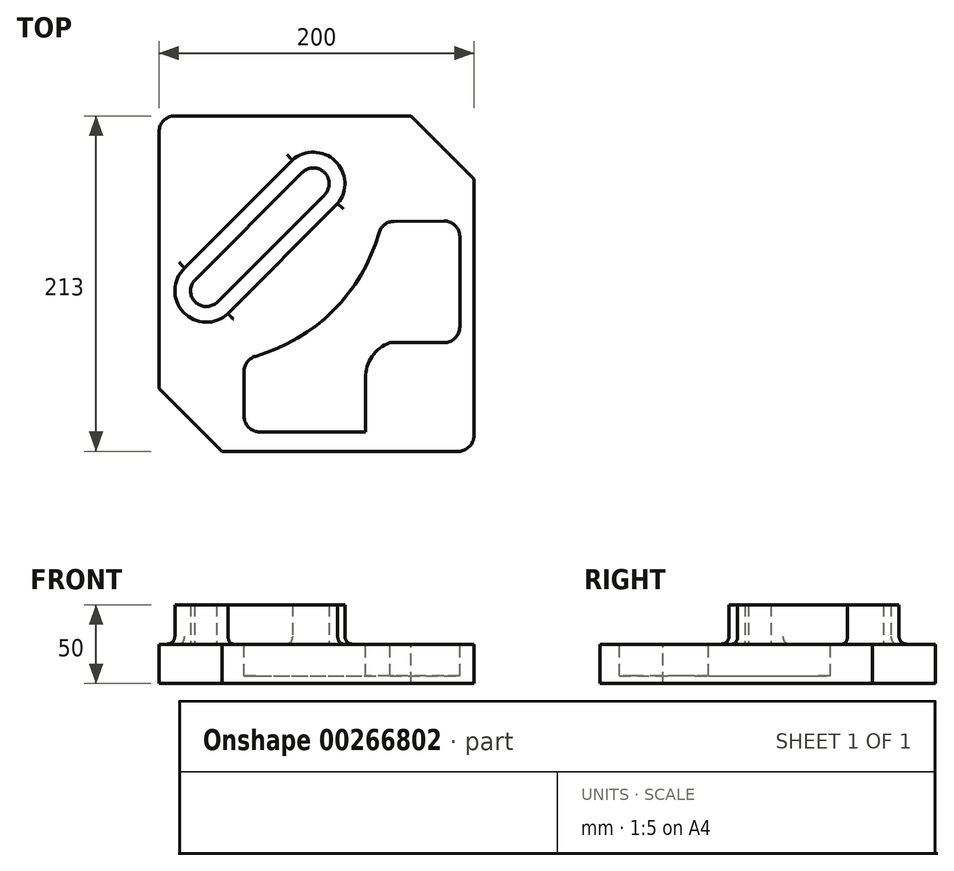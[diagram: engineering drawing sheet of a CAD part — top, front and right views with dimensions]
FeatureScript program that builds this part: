
annotation { "Feature Type Name" : "Feature", "Feature Type Description" : "" }
export const myFeature = defineFeature(function(context is Context, id is Id, definition is map)
    precondition{}
    {
        {
            var Q0;
            Q0=qCreatedBy(makeId("Top.planeOp"),FACE);
            var sketch = newSketch(context, id + "F0", { "sketchPlane" : qUnion([Q0])});
            skLineSegment(sketch, "E0.bottom", {"start": v(-115.8, 100.72) * mm, "end": v(34.2, 100.72) * mm});
            skLineSegment(sketch, "E0.top", {"start": v(-85.8, -112.28) * mm, "end": v(64.2, -112.28) * mm});
            skLineSegment(sketch, "E0.left", {"start": v(-125.8, 90.72) * mm, "end": v(-125.8, -72.28) * mm});
            skLineSegment(sketch, "E0.right", {"start": v(74.2, 60.72) * mm, "end": v(74.2, -102.28) * mm});
            skLineSegment(sketch, "E1", {"start": v(34.2, 100.72) * mm, "end": v(74.2, 60.72) * mm});
            skPoint(sketch, "E2.orphan", {"position": v(74.2, 100.72) * mm});
            skLineSegment(sketch, "E3", {"start": v(-125.8, -72.28) * mm, "end": v(-85.8, -112.28) * mm});
            skPoint(sketch, "E4.orphan", {"position": v(-125.8, -112.28) * mm});
            skPoint(sketch, "E5.visualSharp", {"position": v(-125.8, 100.72) * mm});
            skArc(sketch, "E5.filletArc", {"start": v(-115.8, 100.72) * mm, "mid": v(-122.86, 97.79) * mm, "end": v(-125.8, 90.72) * mm});
            skPoint(sketch, "E6.visualSharp", {"position": v(74.2, -112.28) * mm});
            skArc(sketch, "E6.filletArc", {"start": v(64.2, -112.28) * mm, "mid": v(71.28, -109.36) * mm, "end": v(74.2, -102.28) * mm});
            skArc(sketch, "E7", {"start": v(-20.72, 50.64) * mm, "mid": v(-20.72, 64.79) * mm, "end": v(-34.86, 64.78) * mm});
            skArc(sketch, "E8", {"start": v(-103.36, -3.75) * mm, "mid": v(-102.94, -17.28) * mm, "end": v(-89.43, -18) * mm});
            skLineSegment(sketch, "E9", {"start": v(-103.36, -3.75) * mm, "end": v(-34.86, 64.78) * mm});
            skLineSegment(sketch, "E10", {"start": v(-89.43, -18) * mm, "end": v(-20.72, 50.64) * mm});
            skArc(sketch, "E11", {"start": v(-109.56, 4.22) * mm, "mid": v(-110.3, -24.05) * mm, "end": v(-82.02, -24.8) * mm});
            skArc(sketch, "E12", {"start": v(-12.34, 45.02) * mm, "mid": v(-13.95, 72.16) * mm, "end": v(-41.14, 72.61) * mm});
            skLineSegment(sketch, "E13", {"start": v(-109.56, 4.22) * mm, "end": v(-41.14, 72.61) * mm});
            skLineSegment(sketch, "E14", {"start": v(-82.02, -24.8) * mm, "end": v(-12.34, 45.02) * mm});
            skLineSegment(sketch, "E15", {"start": v(-71.8, -61.53) * mm, "end": v(-71.8, -89.98) * mm});
            skLineSegment(sketch, "E16", {"start": v(-61.8, -99.98) * mm, "end": v(5.2, -99.98) * mm});
            skArc(sketch, "E17", {"start": v(-64.53, -51.92) * mm, "mid": v(-15.16, -22.87) * mm, "end": v(13.86, 26.52) * mm});
            skLineSegment(sketch, "E18", {"start": v(5.2, -99.98) * mm, "end": v(5.2, -65.74) * mm});
            skArc(sketch, "E19", {"start": v(5.2, -65.74) * mm, "mid": v(9.47, -52.09) * mm, "end": v(20.75, -43.28) * mm});
            skLineSegment(sketch, "E20", {"start": v(20.75, -43.28) * mm, "end": v(55.2, -43.28) * mm});
            skLineSegment(sketch, "E21", {"start": v(65.2, -33.28) * mm, "end": v(65.2, 24.06) * mm});
            skLineSegment(sketch, "E22", {"start": v(55.12, 34.06) * mm, "end": v(23.39, 33.78) * mm});
            skPoint(sketch, "E23.visualSharp", {"position": v(-71.8, -99.98) * mm});
            skArc(sketch, "E23.filletArc", {"start": v(-71.8, -89.98) * mm, "mid": v(-68.86, -97.05) * mm, "end": v(-61.8, -99.98) * mm});
            skPoint(sketch, "E24.visualSharp", {"position": v(-71.8, -53.73) * mm});
            skArc(sketch, "E24.filletArc", {"start": v(-64.53, -51.92) * mm, "mid": v(-69.77, -55.5) * mm, "end": v(-71.8, -61.53) * mm});
            skPoint(sketch, "E25.visualSharp", {"position": v(15.65, 33.72) * mm});
            skArc(sketch, "E25.filletArc", {"start": v(23.39, 33.78) * mm, "mid": v(17.42, 31.74) * mm, "end": v(13.86, 26.52) * mm});
            skPoint(sketch, "E26.visualSharp", {"position": v(65.2, 34.15) * mm});
            skArc(sketch, "E26.filletArc", {"start": v(65.2, 24.06) * mm, "mid": v(62.25, 31.16) * mm, "end": v(55.12, 34.06) * mm});
            skPoint(sketch, "E27.visualSharp", {"position": v(65.2, -43.28) * mm});
            skArc(sketch, "E27.filletArc", {"start": v(55.2, -43.28) * mm, "mid": v(62.28, -40.36) * mm, "end": v(65.2, -33.28) * mm});
            skSolve(sketch);
        }
        {
            var Q0;
            Q0=makeQuery(id+"F0.imprint","IMPRINT",FACE,{"disambiguationData":[TD([[makeQuery(id+"F0.imprint","IMPRINT",EDGE,{"derivedFrom":sQuery(id+"F0.wireOp",EDGE,"E0.bottom")}),-1.0]])]});
            var Q1;
            Q1=makeQuery(id+"F0.imprint","IMPRINT",FACE,{"disambiguationData":[TD([[makeQuery(id+"F0.imprint","IMPRINT",EDGE,{"derivedFrom":sQuery(id+"F0.wireOp",EDGE,"E7")}),-1.0]])]});
            var Q2;
            Q2=makeQuery(id+"F0.imprint","IMPRINT",FACE,{"disambiguationData":[TD([[makeQuery(id+"F0.imprint","IMPRINT",EDGE,{"derivedFrom":sQuery(id+"F0.wireOp",EDGE,"E7")}),1.0]])]});
            var Q3;
            Q3=makeQuery(id+"F0.imprint","IMPRINT",FACE,{"disambiguationData":[TD([[makeQuery(id+"F0.imprint","IMPRINT",EDGE,{"derivedFrom":sQuery(id+"F0.wireOp",EDGE,"E15")}),1.0]])]});
            extrude(context, id + "F1", {"entities" : qUnion([Q0, Q1, Q2, Q3]), "oppositeDirection" : true, "depth" : 25 * mm});
        }
        {
            var Q0;
            Q0=makeQuery(id+"F0.imprint","IMPRINT",FACE,{"disambiguationData":[TD([[makeQuery(id+"F0.imprint","IMPRINT",EDGE,{"derivedFrom":sQuery(id+"F0.wireOp",EDGE,"E7")}),-1.0]])]});
            extrude(context, id + "F2", {"entities" : qUnion([Q0]), "operationType" : NewBodyOperationType.ADD, "depth" : 25 * mm});
        }
        {
            var Q0;
            Q0=makeQuery(id+"F0.imprint","IMPRINT",FACE,{"disambiguationData":[TD([[makeQuery(id+"F0.imprint","IMPRINT",EDGE,{"derivedFrom":sQuery(id+"F0.wireOp",EDGE,"E15")}),1.0]])]});
            extrude(context, id + "F3", {"entities" : qUnion([Q0]), "operationType" : NewBodyOperationType.REMOVE, "oppositeDirection" : true, "depth" : 20 * mm});
        }
        {
            var Q0;
            Q0=makeQuery(id+"F2.opExtrude","CAP_EDGE",EDGE,{"disambiguationData":[OSD([sQuery(id+"F0.wireOp",EDGE,"E12")])],"isStart":true});
            fillet(context, id + "F4", {"entities" : qUnion([Q0]), "radius" : 5 * mm, "tangentPropagation" : true, "allowEdgeOverflow" : false});
        }
        {
            var Q0;
            Q0=makeQuery(id+"F2.opExtrude","CAP_EDGE",EDGE,{"disambiguationData":[OSD([sQuery(id+"F0.wireOp",EDGE,"E14")])],"isStart":true});
            var Q1;
            Q1=makeQuery(id+"F3.boolean.opBoolean","COPY",EDGE,{"derivedFrom":makeQuery(id+"F3.opExtrude","CAP_EDGE",EDGE,{"disambiguationData":[OSD([sQuery(id+"F0.wireOp",EDGE,"E20")])],"isStart":true})});
            fillet(context, id + "F5", {"entities" : qUnion([Q0, Q1]), "radius" : 5 * mm, "tangentPropagation" : true, "allowEdgeOverflow" : false});
        }
        {
            var Q0;
            Q0=makeQuery(id+"F2.opExtrude","CAP_EDGE",EDGE,{"disambiguationData":[OSD([sQuery(id+"F0.wireOp",EDGE,"E13")])],"isStart":true});
            fillet(context, id + "F6", {"entities" : qUnion([Q0]), "radius" : 5 * mm, "tangentPropagation" : true, "allowEdgeOverflow" : false});
        }
    });
